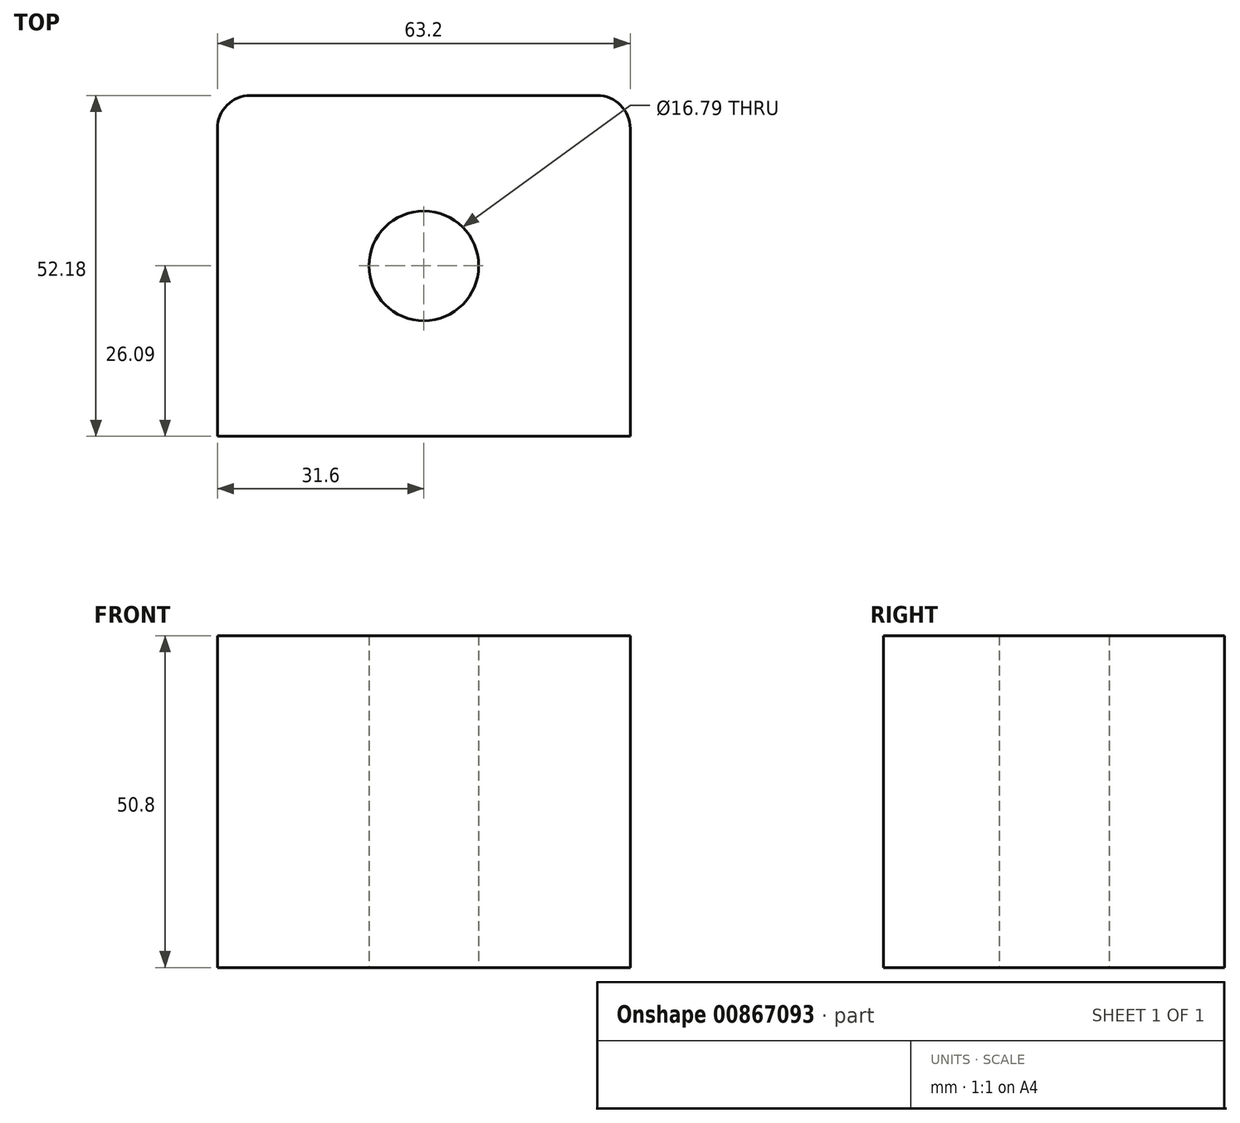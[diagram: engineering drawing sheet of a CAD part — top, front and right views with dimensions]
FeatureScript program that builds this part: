
annotation { "Feature Type Name" : "Feature", "Feature Type Description" : "" }
export const myFeature = defineFeature(function(context is Context, id is Id, definition is map)
    precondition{}
    {
        {
            var Q0;
            Q0=qCreatedBy(makeId("Top.planeOp"),FACE);
            var sketch = newSketch(context, id + "F0", { "sketchPlane" : qUnion([Q0])});
            skLineSegment(sketch, "E0.bottom", {"start": v(31.6, -26.1) * mm, "end": v(-31.6, -26.1) * mm});
            skLineSegment(sketch, "E0.top", {"start": v(31.6, 26.1) * mm, "end": v(-31.6, 26.1) * mm});
            skLineSegment(sketch, "E0.left", {"start": v(31.6, -26.1) * mm, "end": v(31.6, 26.1) * mm});
            skLineSegment(sketch, "E0.right", {"start": v(-31.6, -26.1) * mm, "end": v(-31.6, 26.1) * mm});
            skPoint(sketch, "E0.middle", {"position": v(0, 0) * mm});
            skCircle(sketch, "E1", {"center": v(0, 0) * mm, "radius": 8.4 * mm});
            skSolve(sketch);
        }
        {
            var Q0;
            Q0=makeQuery(id+"F0.imprint","IMPRINT",FACE,{"disambiguationData":[TD([[makeQuery(id+"F0.imprint","IMPRINT",EDGE,{"derivedFrom":sQuery(id+"F0.wireOp",EDGE,"E0.bottom")}),-1.0]])]});
            extrude(context, id + "F1", {"entities" : qUnion([Q0]), "depth" : 25.4 * mm, "offsetDistance" : 25.4 * mm, "hasSecondDirection" : true, "secondDirectionOppositeDirection" : true, "secondDirectionDepth" : 25.4 * mm});
        }
        {
            var Q0;
            Q0=makeQuery(id+"F1.opExtrude","SWEPT_EDGE",EDGE,{"disambiguationData":[OSD([sQuery(id+"F0.wireOp",EDGE,"E0.top"),sQuery(id+"F0.wireOp",EDGE,"E0.right")])]});
            var Q1;
            Q1=makeQuery(id+"F1.opExtrude","SWEPT_EDGE",EDGE,{"disambiguationData":[OSD([sQuery(id+"F0.wireOp",EDGE,"E0.top"),sQuery(id+"F0.wireOp",EDGE,"E0.left")])]});
            fillet(context, id + "F2", {"entities" : qUnion([Q0, Q1]), "radius" : 5.08 * mm, "tangentPropagation" : true, "allowEdgeOverflow" : false});
        }
        {
            var Q0;
            Q0=makeQuery(id+"F1.opExtrude","SWEPT_FACE",FACE,{"disambiguationData":[OSD([sQuery(id+"F0.wireOp",EDGE,"E0.right")])]});
            var sketch = newSketch(context, id + "F3", { "sketchPlane" : qUnion([Q0])});
            skCircle(sketch, "E2", {"center": v(0, 0) * mm, "radius": 17.64 * mm});
            skSolve(sketch);
        }
        {
            var Q0;
            Q0=sQuery(id+"F3.wireOp",EDGE,"E2");
            extrude(context, id + "F4", {"bodyType" : ToolBodyType.SURFACE, "surfaceEntities" : qUnion([Q0]), "depth" : 127 * mm, "offsetDistance" : 25.4 * mm});
        }
    });
